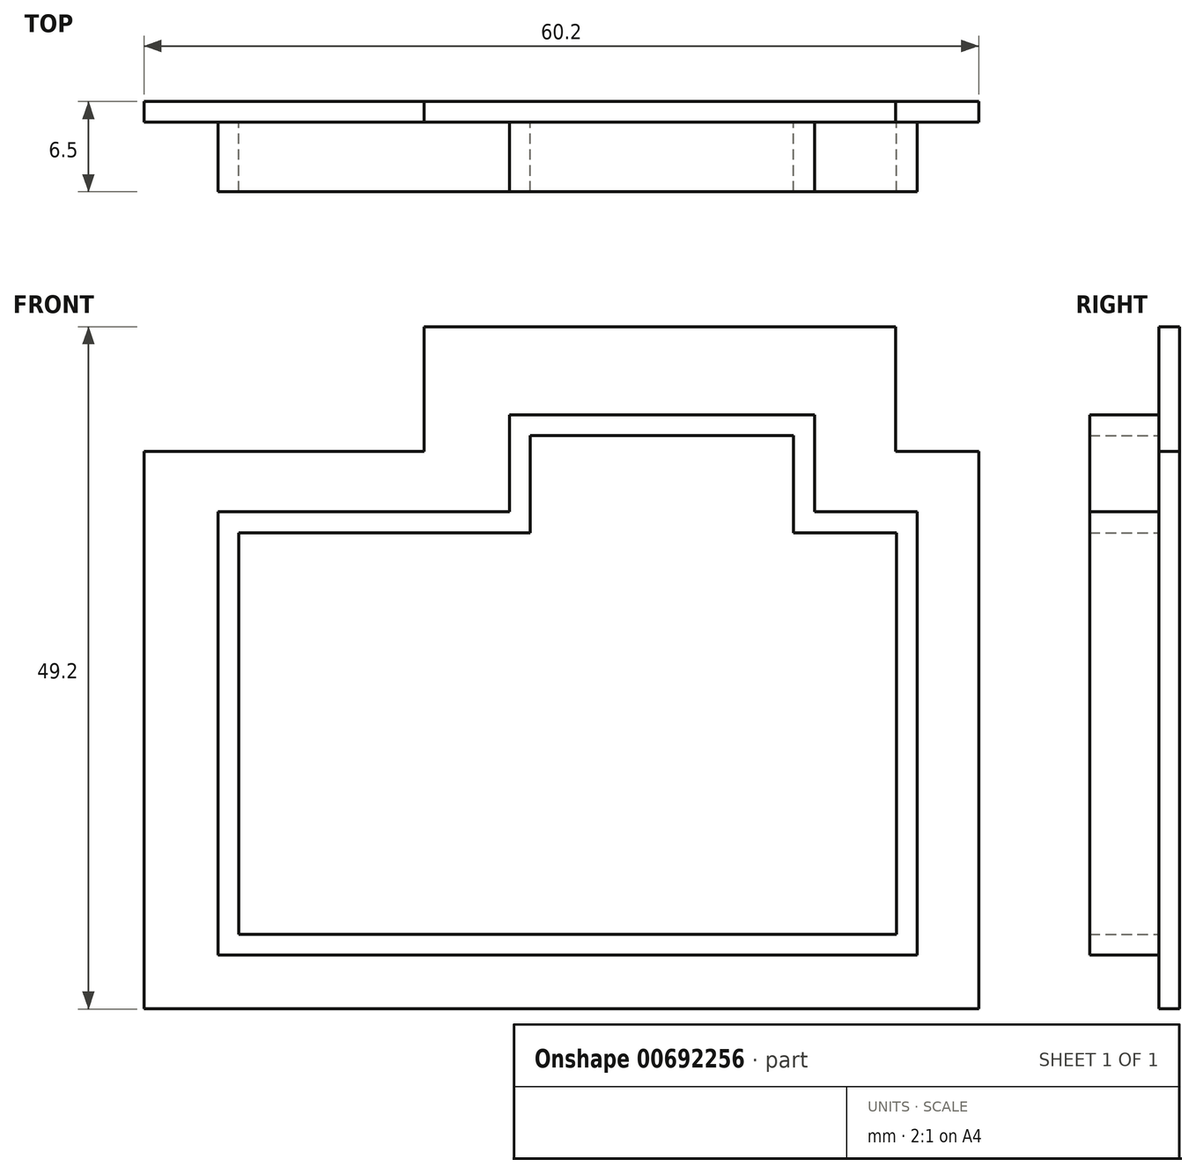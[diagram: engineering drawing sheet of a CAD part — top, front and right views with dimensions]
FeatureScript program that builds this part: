
annotation { "Feature Type Name" : "Feature", "Feature Type Description" : "" }
export const myFeature = defineFeature(function(context is Context, id is Id, definition is map)
    precondition{}
    {
        {
            var Q0;
            Q0=qCreatedBy(makeId("Front.planeOp"),FACE);
            var sketch = newSketch(context, id + "F0", { "sketchPlane" : qUnion([Q0])});
            skLineSegment(sketch, "E0", {"start": v(-52.33, -14.85) * mm, "end": v(7.87, -14.85) * mm});
            skLineSegment(sketch, "E1", {"start": v(7.87, -14.85) * mm, "end": v(7.87, 25.35) * mm});
            skLineSegment(sketch, "E2", {"start": v(7.87, 25.35) * mm, "end": v(1.87, 25.35) * mm});
            skLineSegment(sketch, "E3", {"start": v(1.87, 25.35) * mm, "end": v(1.87, 34.35) * mm});
            skLineSegment(sketch, "E4", {"start": v(1.87, 34.35) * mm, "end": v(-32.13, 34.35) * mm});
            skLineSegment(sketch, "E5", {"start": v(-32.13, 34.35) * mm, "end": v(-32.13, 25.35) * mm});
            skLineSegment(sketch, "E6", {"start": v(-32.13, 25.35) * mm, "end": v(-52.33, 25.35) * mm});
            skLineSegment(sketch, "E7", {"start": v(-52.33, -14.85) * mm, "end": v(-52.33, 25.35) * mm});
            skSolve(sketch);
        }
        {
            var Q0;
            Q0 = qSketchRegion(id + "F0", true);
            extrude(context, id + "F1", {"entities" : qUnion([Q0]), "depth" : 1.5 * mm, "offsetDistance" : 25 * mm});
        }
        {
            var Q0;
            Q0=makeQuery(id+"F1.opExtrude","CAP_FACE",FACE,{"disambiguationData":[OSD([sQuery(id+"F0.wireOp",EDGE,"E0"),sQuery(id+"F0.wireOp",EDGE,"E1"),sQuery(id+"F0.wireOp",EDGE,"E2"),sQuery(id+"F0.wireOp",EDGE,"E3"),sQuery(id+"F0.wireOp",EDGE,"E4"),sQuery(id+"F0.wireOp",EDGE,"E5"),sQuery(id+"F0.wireOp",EDGE,"E6"),sQuery(id+"F0.wireOp",EDGE,"E7")])],"isStart":false});
            var sketch = newSketch(context, id + "F2", { "sketchPlane" : qUnion([Q0])});
            skLineSegment(sketch, "E8", {"start": v(-46.98, -10.97) * mm, "end": v(3.44, -10.97) * mm});
            skLineSegment(sketch, "E9", {"start": v(3.44, 21) * mm, "end": v(3.44, -10.97) * mm});
            skLineSegment(sketch, "E10", {"start": v(3.44, 21) * mm, "end": v(-3.98, 21) * mm});
            skLineSegment(sketch, "E11", {"start": v(-3.98, 28) * mm, "end": v(-25.98, 28) * mm});
            skLineSegment(sketch, "E12", {"start": v(-25.98, 28) * mm, "end": v(-3.98, 28) * mm});
            skLineSegment(sketch, "E13", {"start": v(-3.98, 28) * mm, "end": v(-3.98, 21) * mm});
            skLineSegment(sketch, "E14", {"start": v(-25.98, 28) * mm, "end": v(-25.98, 21) * mm});
            skLineSegment(sketch, "E15", {"start": v(-46.98, 21) * mm, "end": v(-25.98, 21) * mm});
            skLineSegment(sketch, "E16", {"start": v(-46.98, -10.97) * mm, "end": v(-46.98, 21) * mm});
            skSolve(sketch);
        }
        {
            var Q0;
            Q0 = qSketchRegion(id + "F2", true);
            extrude(context, id + "F3", {"entities" : qUnion([Q0]), "operationType" : NewBodyOperationType.ADD, "depth" : 5 * mm, "offsetDistance" : 25 * mm});
        }
        {
            var Q0;
            Q0=makeQuery(id+"F3.opExtrude","CAP_FACE",FACE,{"disambiguationData":[OSD([sQuery(id+"F2.wireOp",EDGE,"E8"),sQuery(id+"F2.wireOp",EDGE,"E9"),sQuery(id+"F2.wireOp",EDGE,"E10"),sQuery(id+"F2.wireOp",EDGE,"E12"),sQuery(id+"F2.wireOp",EDGE,"E13"),sQuery(id+"F2.wireOp",EDGE,"E14"),sQuery(id+"F2.wireOp",EDGE,"E15"),sQuery(id+"F2.wireOp",EDGE,"E16")])],"isStart":false});
            shell(context, id + "F4", {"entities" : qUnion([Q0]), "thickness" : 1.5 * mm});
        }
    });
